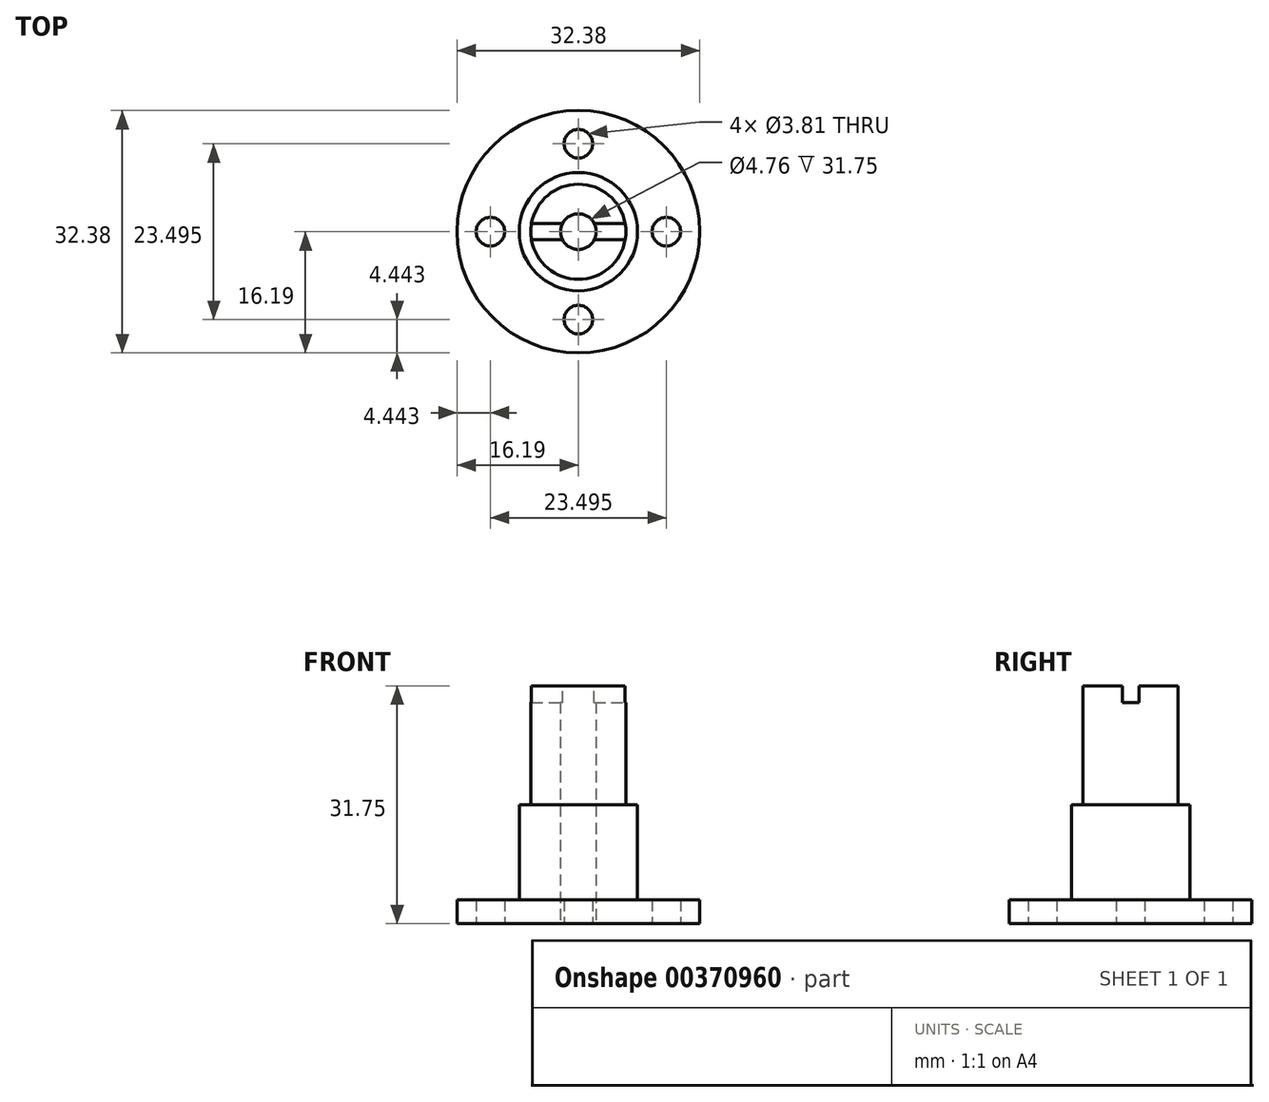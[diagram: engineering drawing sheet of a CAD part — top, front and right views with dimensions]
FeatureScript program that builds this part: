
annotation { "Feature Type Name" : "Feature", "Feature Type Description" : "" }
export const myFeature = defineFeature(function(context is Context, id is Id, definition is map)
    precondition{}
    {
        {
            var Q0;
            Q0=qCreatedBy(makeId("Top.planeOp"),FACE);
            var sketch = newSketch(context, id + "F0", { "sketchPlane" : qUnion([Q0])});
            skCircle(sketch, "E0", {"center": v(0, 0) * mm, "radius": 2.38 * mm});
            skCircle(sketch, "E1", {"center": v(0, 0) * mm, "radius": 6.35 * mm});
            skCircle(sketch, "E2", {"center": v(0, 0) * mm, "radius": 16.2 * mm});
            skCircle(sketch, "E3", {"center": v(0, 0) * mm, "radius": 11.75 * mm, "construction": true});
            skLineSegment(sketch, "E4", {"start": v(0, 0) * mm, "end": v(0, 12.88) * mm, "construction": true});
            skLineSegment(sketch, "E5", {"start": v(0, 0) * mm, "end": v(13.44, 0) * mm, "construction": true});
            skLineSegment(sketch, "E6", {"start": v(0, 0) * mm, "end": v(0, -11.5) * mm, "construction": true});
            skLineSegment(sketch, "E7", {"start": v(0, 0) * mm, "end": v(-13.18, 0) * mm, "construction": true});
            skCircle(sketch, "E8", {"center": v(-11.75, 0) * mm, "radius": 1.9 * mm});
            skCircle(sketch, "E9", {"center": v(11.75, 0) * mm, "radius": 1.9 * mm});
            skCircle(sketch, "E10", {"center": v(0, -11.75) * mm, "radius": 1.9 * mm});
            skCircle(sketch, "E11", {"center": v(0, 11.75) * mm, "radius": 1.9 * mm});
            skCircle(sketch, "E12", {"center": v(0, 0) * mm, "radius": 7.9 * mm});
            skSolve(sketch);
        }
        {
            var Q0;
            Q0=makeQuery(id+"F0.imprint","IMPRINT",FACE,{"disambiguationData":[TD([[makeQuery(id+"F0.imprint","IMPRINT",EDGE,{"derivedFrom":sQuery(id+"F0.wireOp",EDGE,"E1")}),-1.0]])]});
            extrude(context, id + "F1", {"entities" : qUnion([Q0]), "depth" : 15.88 * mm});
        }
        {
            var Q0;
            Q0=makeQuery(id+"F0.imprint","IMPRINT",FACE,{"disambiguationData":[TD([[makeQuery(id+"F0.imprint","IMPRINT",EDGE,{"derivedFrom":sQuery(id+"F0.wireOp",EDGE,"E0")}),-1.0]])]});
            extrude(context, id + "F2", {"entities" : qUnion([Q0]), "operationType" : NewBodyOperationType.ADD, "offsetDistance" : 25.4 * mm, "depth" : 31.75 * mm});
        }
        {
            var Q0;
            Q0=makeQuery(id+"F2.opExtrude","CAP_FACE",FACE,{"disambiguationData":[OSD([sQuery(id+"F0.wireOp",EDGE,"E0"),sQuery(id+"F0.wireOp",EDGE,"E1")])],"isStart":false});
            var sketch = newSketch(context, id + "F3", { "sketchPlane" : qUnion([Q0])});
            skPoint(sketch, "E13", {"position": v(0.93, 6.28) * mm});
            skSolve(sketch);
        }
        {
            var Q0;
            Q0=makeQuery(id+"F0.imprint","IMPRINT",FACE,{"disambiguationData":[TD([[makeQuery(id+"F0.imprint","IMPRINT",EDGE,{"derivedFrom":sQuery(id+"F0.wireOp",EDGE,"E2")}),1.0]])]});
            extrude(context, id + "F4", {"entities" : qUnion([Q0]), "operationType" : NewBodyOperationType.ADD, "offsetDistance" : 25.4 * mm, "depth" : 3.17 * mm});
        }
        {
            var Q0;
            Q0=makeQuery(id+"F3.imprint","IMPRINT",FACE,{"disambiguationData":[TD([[makeQuery(id+"F3.imprint","IMPRINT",EDGE,{"derivedFrom":makeQuery(id+"F2.opExtrude","CAP_EDGE",EDGE,{"disambiguationData":[OSD([sQuery(id+"F0.wireOp",EDGE,"E0")])],"isStart":false})}),-1.0]])]});
            var sketch = newSketch(context, id + "F5", { "sketchPlane" : qUnion([Q0])});
            skLineSegment(sketch, "E14.bottom", {"start": v(-6.25, 1.1) * mm, "end": v(6.25, 1.1) * mm});
            skLineSegment(sketch, "E14.top", {"start": v(-6.25, -1.1) * mm, "end": v(6.25, -1.1) * mm});
            skPoint(sketch, "E14.middle", {"position": v(0, 0) * mm});
            skSolve(sketch);
        }
        {
            var Q0;
            {var subQ0=sQuery(id+"F5.wireOp",EDGE,"E14.bottom");var subQ1=makeQuery(id+"F3.imprint","IMPRINT",EDGE,{"derivedFrom":makeQuery(id+"F2.opExtrude","CAP_EDGE",EDGE,{"disambiguationData":[OSD([sQuery(id+"F0.wireOp",EDGE,"E1")])],"isStart":false})});var subQ2=makeQuery(id+"F5.imprint","INTERSECT",VERTEX,{"disambiguationData":[OD(0.0)],"derivedFrom":[subQ1,subQ0]});Q0=makeQuery(id+"F5.imprint","IMPRINT",FACE,{"disambiguationData":[TD([[makeQuery(id+"F5.imprint","IMPRINT",EDGE,{"disambiguationData":[TD([[subQ2,-1.0]])],"derivedFrom":subQ0}),-1.0]])]});}
            var Q1;
            {var subQ0=sQuery(id+"F5.wireOp",EDGE,"E14.bottom");var subQ1=makeQuery(id+"F3.imprint","IMPRINT",EDGE,{"derivedFrom":makeQuery(id+"F2.opExtrude","CAP_EDGE",EDGE,{"disambiguationData":[OSD([sQuery(id+"F0.wireOp",EDGE,"E1")])],"isStart":false})});var subQ2=makeQuery(id+"F5.imprint","INTERSECT",VERTEX,{"disambiguationData":[OD(1.0)],"derivedFrom":[subQ1,subQ0]});Q1=makeQuery(id+"F5.imprint","IMPRINT",FACE,{"disambiguationData":[TD([[makeQuery(id+"F5.imprint","IMPRINT",EDGE,{"disambiguationData":[TD([[subQ2,1.0]])],"derivedFrom":subQ0}),-1.0]])]});}
            extrude(context, id + "F6", {"entities" : qUnion([Q0, Q1]), "operationType" : NewBodyOperationType.REMOVE, "oppositeDirection" : true, "depth" : 2.2 * mm});
        }
    });
